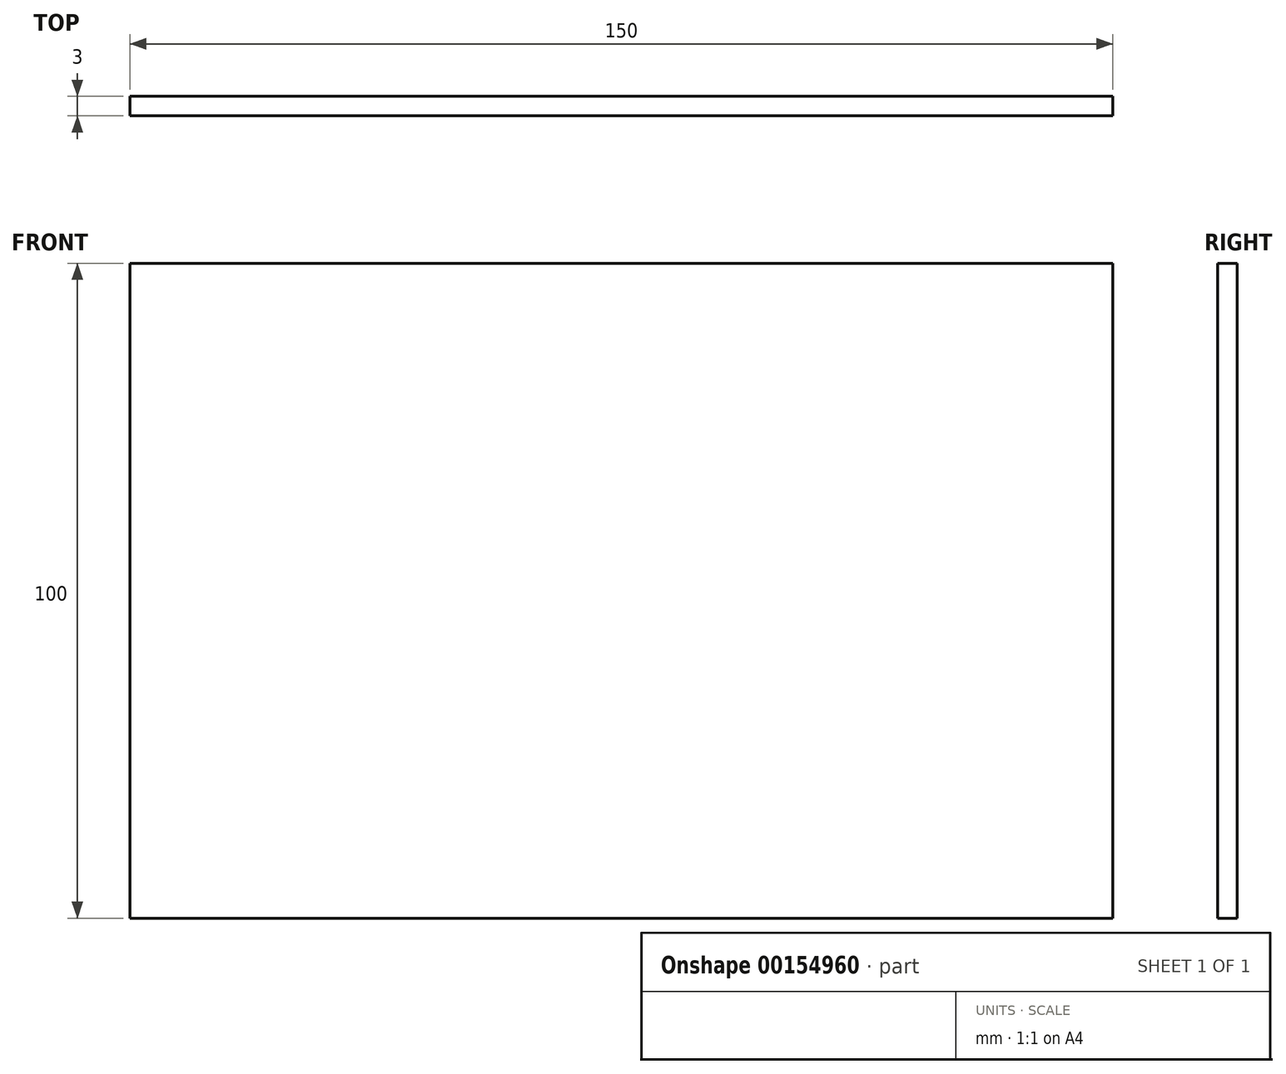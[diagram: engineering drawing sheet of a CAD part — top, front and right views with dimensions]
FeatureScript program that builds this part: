
annotation { "Feature Type Name" : "Feature", "Feature Type Description" : "" }
export const myFeature = defineFeature(function(context is Context, id is Id, definition is map)
    precondition{}
    {
        {
            var Q0;
            Q0=qCreatedBy(makeId("Front.planeOp"),FACE);
            var sketch = newSketch(context, id + "F0", { "sketchPlane" : qUnion([Q0])});
            skLineSegment(sketch, "E0.bottom", {"start": v(76, 50) * mm, "end": v(-74, 50) * mm});
            skLineSegment(sketch, "E0.top", {"start": v(76, -50) * mm, "end": v(-74, -50) * mm});
            skLineSegment(sketch, "E0.left", {"start": v(76, 50) * mm, "end": v(76, -50) * mm});
            skLineSegment(sketch, "E0.right", {"start": v(-74, 50) * mm, "end": v(-74, -50) * mm});
            skPoint(sketch, "E0.middle", {"position": v(1, 0) * mm});
            skSolve(sketch);
        }
        {
            var Q0;
            Q0=makeQuery(id+"F0.imprint","IMPRINT",FACE,{"disambiguationData":[TD([[makeQuery(id+"F0.imprint","IMPRINT",EDGE,{"derivedFrom":sQuery(id+"F0.wireOp",EDGE,"E0.bottom")}),1.0]])]});
            extrude(context, id + "F1", {"entities" : qUnion([Q0]), "depth" : 3 * mm});
        }
    });
